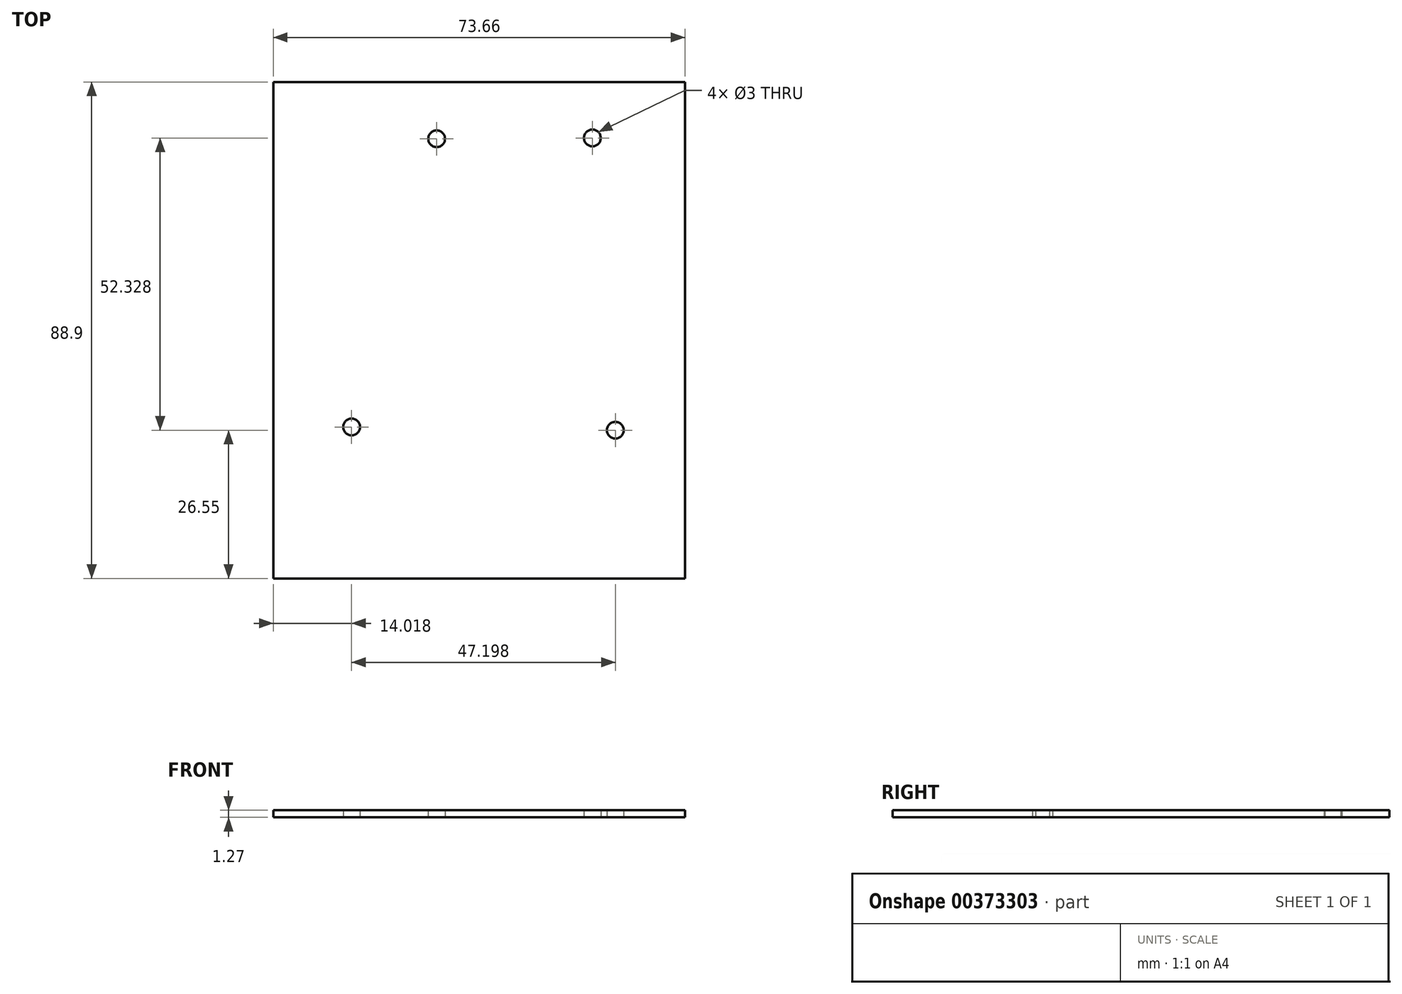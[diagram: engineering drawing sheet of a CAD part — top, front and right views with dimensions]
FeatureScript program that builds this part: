
annotation { "Feature Type Name" : "Feature", "Feature Type Description" : "" }
export const myFeature = defineFeature(function(context is Context, id is Id, definition is map)
    precondition{}
    {
        {
            var Q0;
            Q0=qCreatedBy(makeId("Top.planeOp"),FACE);
            var sketch = newSketch(context, id + "F0", { "sketchPlane" : qUnion([Q0])});
            skLineSegment(sketch, "E0.bottom", {"start": v(-38.42, 37.96) * mm, "end": v(35.24, 37.96) * mm});
            skLineSegment(sketch, "E0.top", {"start": v(-38.42, -50.94) * mm, "end": v(35.24, -50.94) * mm});
            skLineSegment(sketch, "E0.left", {"start": v(-38.42, 37.96) * mm, "end": v(-38.42, -50.94) * mm});
            skLineSegment(sketch, "E0.right", {"start": v(35.24, 37.96) * mm, "end": v(35.24, -50.94) * mm});
            skPoint(sketch, "E1", {"position": v(-9.18, 27.8) * mm});
            skPoint(sketch, "E2", {"position": v(18.69, 27.94) * mm});
            skPoint(sketch, "E3", {"position": v(22.8, -24.39) * mm});
            skPoint(sketch, "E4", {"position": v(-24.4, -23.8) * mm});
            skSolve(sketch);
        }
        {
            var Q0;
            Q0=makeQuery(id+"F0.imprint","IMPRINT",FACE,{"disambiguationData":[TD([[makeQuery(id+"F0.imprint","IMPRINT",EDGE,{"derivedFrom":sQuery(id+"F0.wireOp",EDGE,"E0.bottom")}),-1.0]])]});
            extrude(context, id + "F1", {"entities" : qUnion([Q0]), "depth" : 1.27 * mm});
        }
        {
            var Q0;
            Q0=sQuery(id+"F0.wireOp",VERTEX,"E1");
            var Q1;
            Q1=sQuery(id+"F0.wireOp",VERTEX,"E2");
            var Q2;
            Q2=sQuery(id+"F0.wireOp",VERTEX,"E3");
            var Q3;
            Q3=sQuery(id+"F0.wireOp",VERTEX,"E4");
            var Q4;
            Q4=makeQuery(id+"F1.opExtrude","SWEPT_BODY",BODY,{"disambiguationData":[OSD([sQuery(id+"F0.wireOp",EDGE,"E0.bottom"),sQuery(id+"F0.wireOp",EDGE,"E0.top"),sQuery(id+"F0.wireOp",EDGE,"E0.left"),sQuery(id+"F0.wireOp",EDGE,"E0.right")])]});
            hole(context, id + "F2", {"style" : HoleStyle.SIMPLE, "endStyle" : HoleEndStyle.THROUGH, "oppositeDirection" : true, "holeDiameter" : 3 * mm, "isTappedThrough" : true, "tappedDepth" : 12.7 * mm, "tapClearance" : 3, "locations" : qUnion([Q0, Q1, Q2, Q3]), "scope" : qUnion([Q4])});
        }
    });
